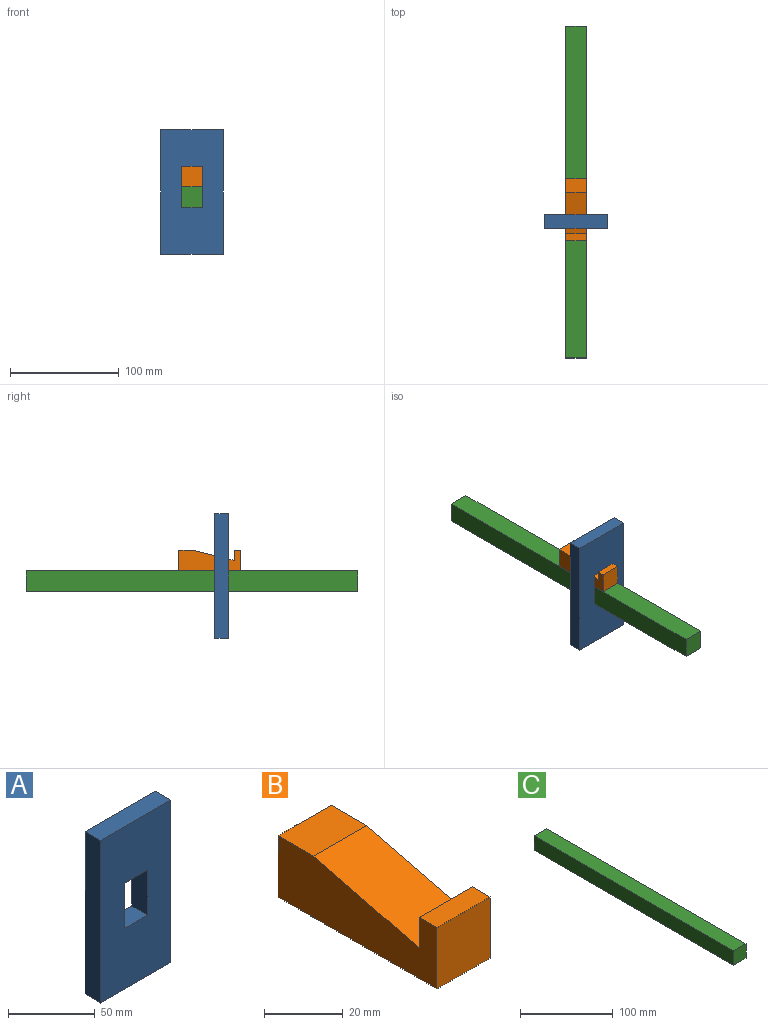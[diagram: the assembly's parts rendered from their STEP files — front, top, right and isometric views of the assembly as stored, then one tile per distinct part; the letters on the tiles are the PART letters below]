
ASSEMBLY  parts=3 mates=2
PART A: 10 faces, bbox 57.2x12.7x114.3 mm
  f0: plane 114.3x57.15mm, normal (0,-1,0), area 5927.4mm2, adj f1,f2,f3,f4,f5,f7,f8,f9
  f1: plane 34.3x12.7mm, normal (-1,0,0), area 419.4mm2, adj f0,f2,f6,f7
  f2: plane 19.05x12.7mm, normal (0,0,1), area 241.9mm2, adj f0,f1,f6,f8
  f3: plane 57.15x12.7mm, normal (0,0,-1), area 725.8mm2, adj f0,f4,f6,f9
  f4: plane 114.3x12.7mm, normal (1,0,0), area 1451.6mm2, adj f0,f3,f5,f6
  f5: plane 57.15x12.7mm, normal (0,0,1), area 725.8mm2, adj f0,f4,f6,f9
  f6: plane 114.3x57.15mm, normal (0,1,0), area 5878.8mm2, adj f1,f2,f3,f4,f5,f7,f8,f9
  f7: plane 19.05x12.7mm, normal (0,0.2,-0.98), area 246.8mm2, adj f0,f1,f6,f8
  f8: plane 34.3x12.7mm, normal (1,0,0), area 419.4mm2, adj f0,f2,f6,f7
  f9: plane 114.3x12.7mm, normal (-1,0,0), area 1451.6mm2, adj f0,f3,f5,f6
PART B: 9 faces, bbox 19.1x57.2x19.1 mm
  f0: plane 19.05x19.05mm, normal (0,-1,0), area 362.9mm2, adj f1,f6,f7,f8
  f1: plane 19.05x6.35mm, normal (0,0,1), area 121mm2, adj f0,f2,f7,f8
  f2: plane 19.05x9.53mm, normal (0,1,0), area 181.5mm2, adj f1,f3,f7,f8
  f3: plane 38.1x19.05mm, normal (0,-0.24,0.97), area 748.1mm2, adj f2,f4,f7,f8
  f4: plane 19.05x12.7mm, normal (0,0,1), area 241.9mm2, adj f3,f5,f7,f8
  f5: plane 19.05x19.05mm, normal (0,1,0), area 362.9mm2, adj f4,f6,f7,f8
  f6: plane 57.15x19.05mm, normal (0,0,-1), area 1088.7mm2, adj f0,f5,f7,f8
  f7: plane 57.15x19.05mm, normal (1,0,0), area 907.3mm2, adj f0,f1,f2,f3,f4,f5,f6
  f8: plane 57.15x19.05mm, normal (-1,0,0), area 907.3mm2, adj f0,f1,f2,f3,f4,f5,f6
PART C: 6 faces, bbox 19.1x304.8x19.1 mm
  f0: plane 304.8x19.05mm, normal (1,0,0), area 5806.4mm2, adj f1,f3,f4,f5
  f1: plane 304.8x19.05mm, normal (0,0,1), area 5806.4mm2, adj f0,f2,f4,f5
  f2: plane 304.8x19.05mm, normal (-1,0,0), area 5806.4mm2, adj f1,f3,f4,f5
  f3: plane 304.8x19.05mm, normal (0,0,-1), area 5806.4mm2, adj f0,f2,f4,f5
  f4: plane 19.05x19.05mm, normal (0,-1,0), area 362.9mm2, adj f0,f1,f2,f3
  f5: plane 19.05x19.05mm, normal (0,1,0), area 362.9mm2, adj f0,f1,f2,f3
PLACE A t=(-28.58,0,57.15)mm
PLACE B t=(-28.58,2.31,57.15)mm
PLACE C t=(-28.58,20.84,57.15)mm
MATE slider C.f5 <-> A.f6  axis (0,1,0) through (-28.58,173.24,42.86)mm
MATE slider B.f5 <-> C.f5  axis (0,1,0) through (-28.58,33.04,61.91)mm
